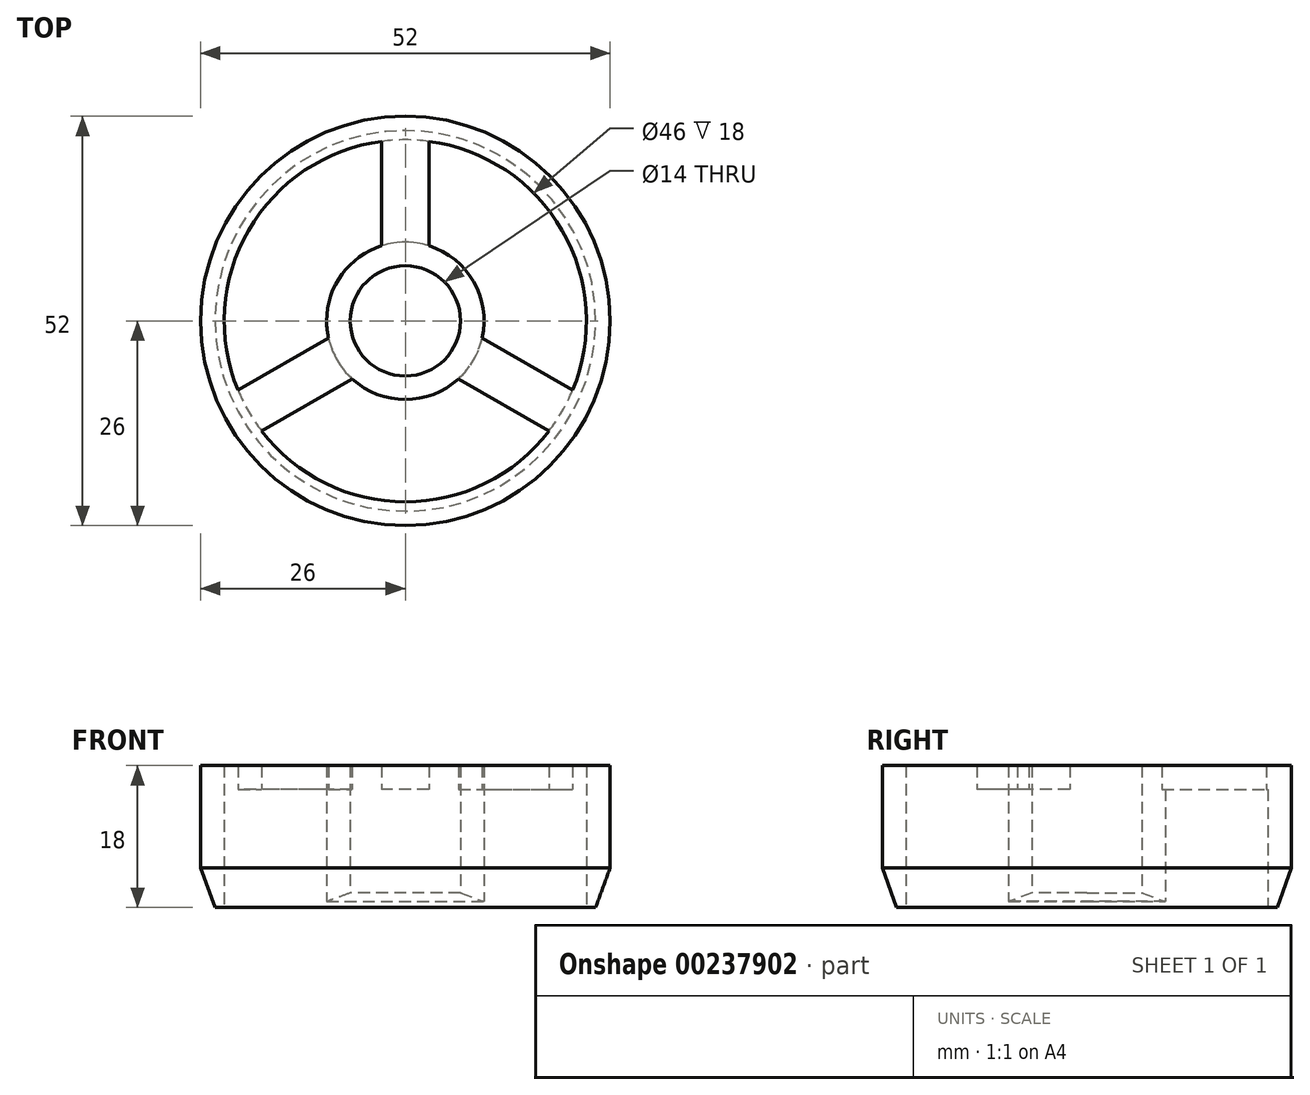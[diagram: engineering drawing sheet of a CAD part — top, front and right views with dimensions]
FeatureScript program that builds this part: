
annotation { "Feature Type Name" : "Feature", "Feature Type Description" : "" }
export const myFeature = defineFeature(function(context is Context, id is Id, definition is map)
    precondition{}
    {
        {
            var Q0;
            Q0=qCreatedBy(makeId("Top.planeOp"),FACE);
            var sketch = newSketch(context, id + "F0", { "sketchPlane" : qUnion([Q0])});
            skCircle(sketch, "E0", {"center": v(0, 0) * mm, "radius": 23 * mm});
            skCircle(sketch, "E1", {"center": v(0, 0) * mm, "radius": 26 * mm});
            skCircle(sketch, "E2", {"center": v(0, 0) * mm, "radius": 10 * mm});
            skCircle(sketch, "E3", {"center": v(0, 0) * mm, "radius": 7 * mm});
            skLineSegment(sketch, "E4", {"start": v(-3, 9.54) * mm, "end": v(-3, 22.8) * mm});
            skLineSegment(sketch, "E5", {"start": v(3, 9.54) * mm, "end": v(3, 22.8) * mm});
            skLineSegment(sketch, "E6.1.0", {"start": v(-9.76, -2.17) * mm, "end": v(-21.25, -8.8) * mm});
            skLineSegment(sketch, "E6.1.1", {"start": v(-6.76, -7.37) * mm, "end": v(-18.25, -14) * mm});
            skLineSegment(sketch, "E6.2.0", {"start": v(6.76, -7.37) * mm, "end": v(18.25, -14) * mm});
            skLineSegment(sketch, "E6.2.1", {"start": v(9.76, -2.17) * mm, "end": v(21.25, -8.8) * mm});
            skSolve(sketch);
        }
        {
            var Q0;
            Q0=makeQuery(id+"F0.imprint","IMPRINT",FACE,{"disambiguationData":[TD([[makeQuery(id+"F0.imprint","IMPRINT",EDGE,{"derivedFrom":sQuery(id+"F0.wireOp",EDGE,"E1")}),1.0]])]});
            var Q1;
            {var subQ0=sQuery(id+"F0.wireOp",EDGE,"E6.1.0");Q1=makeQuery(id+"F0.imprint","IMPRINT",FACE,{"disambiguationData":[TD([[makeQuery(id+"F0.imprint","IMPRINT",EDGE,{"derivedFrom":subQ0}),1.0]])]});}
            var Q2;
            Q2=makeQuery(id+"F0.imprint","IMPRINT",FACE,{"disambiguationData":[TD([[makeQuery(id+"F0.imprint","IMPRINT",EDGE,{"derivedFrom":sQuery(id+"F0.wireOp",EDGE,"E3")}),-1.0]])]});
            var Q3;
            {var subQ0=sQuery(id+"F0.wireOp",EDGE,"E4");Q3=makeQuery(id+"F0.imprint","IMPRINT",FACE,{"disambiguationData":[TD([[makeQuery(id+"F0.imprint","IMPRINT",EDGE,{"derivedFrom":subQ0}),-1.0]])]});}
            var Q4;
            {var subQ0=sQuery(id+"F0.wireOp",EDGE,"E6.2.0");Q4=makeQuery(id+"F0.imprint","IMPRINT",FACE,{"disambiguationData":[TD([[makeQuery(id+"F0.imprint","IMPRINT",EDGE,{"derivedFrom":subQ0}),1.0]])]});}
            extrude(context, id + "F1", {"entities" : qUnion([Q0, Q1, Q2, Q3, Q4]), "depth" : 3 * mm, "offsetDistance" : 25 * mm});
        }
        {
            var Q0;
            Q0=makeQuery(id+"F0.imprint","IMPRINT",FACE,{"disambiguationData":[TD([[makeQuery(id+"F0.imprint","IMPRINT",EDGE,{"derivedFrom":sQuery(id+"F0.wireOp",EDGE,"E1")}),1.0]])]});
            var Q1;
            Q1=makeQuery(id+"F0.imprint","IMPRINT",FACE,{"disambiguationData":[TD([[makeQuery(id+"F0.imprint","IMPRINT",EDGE,{"derivedFrom":sQuery(id+"F0.wireOp",EDGE,"E3")}),-1.0]])]});
            extrude(context, id + "F2", {"entities" : qUnion([Q0, Q1]), "operationType" : NewBodyOperationType.ADD, "oppositeDirection" : true, "depth" : 15 * mm, "offsetDistance" : 25 * mm});
        }
        {
            var Q0;
            Q0=makeQuery(id+"F2.opExtrude","CAP_EDGE",EDGE,{"disambiguationData":[OSD([sQuery(id+"F0.wireOp",EDGE,"E1")])],"isStart":false});
            chamfer(context, id + "F3", {"entities" : qUnion([Q0]), "chamferType" : ChamferType.OFFSET_ANGLE, "width" : 5 * mm, "oppositeDirection" : false, "angle" : 20 * degree, "tangentPropagation" : true});
        }
        {
            var Q0;
            Q0=makeQuery(id+"F2.opExtrude","CAP_EDGE",EDGE,{"disambiguationData":[OSD([sQuery(id+"F0.wireOp",EDGE,"E3")])],"isStart":false});
            chamfer(context, id + "F4", {"entities" : qUnion([Q0]), "chamferType" : ChamferType.OFFSET_ANGLE, "width" : 5 * mm, "oppositeDirection" : true, "angle" : 20 * degree, "tangentPropagation" : true});
        }
    });
